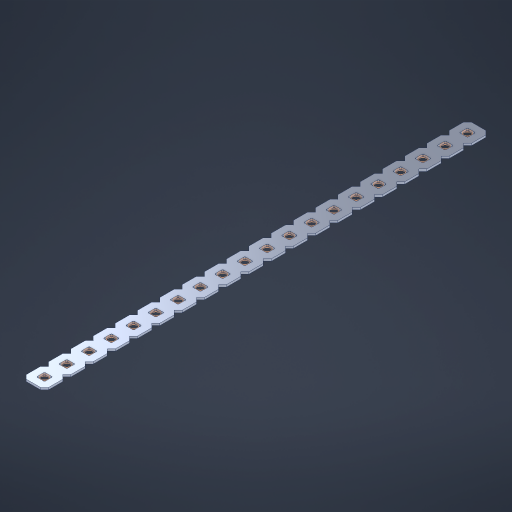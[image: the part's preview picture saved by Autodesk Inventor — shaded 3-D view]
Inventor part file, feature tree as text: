
AUTODESK INVENTOR PART (.ipt)
format: ipt  version: 2023 (Build 270158000, 158)  size: 516,608 bytes
history: native  units: in
note: dims shown in document units (in); Inventor stores cm internally (conversion verified against a paired STEP export)
features: other x21, extrude x19, sketch x2, pattern_linear x1
ambient origin geometry x8: Origin, YZ Plane, XZ Plane, XY Plane, X Axis, Y Axis, Z Axis, Center Point
bodies: Solid1 (feature_tree), Body (feature_tree)
feature tree (43):
  pattern_linear  "Rectangular Pattern1"  Spacing1=0.09in  [1 undecoded]
  sketch  "Sketch1"  dims[d1=0.5in]
  sketch  "Sketch2"  dims[d2=0.182in d3=0.09in d4=0.09in d5=0.09in d6=0.09in d7=0.09in d8=0.09in d9=0.09in d10=0.09in d11=0.02in d13=0.0in d14=0.172in d15=0.0625in d16=0.0in d19=0.5in d22=0.5in]
  other  "Srf1"
  other  "Srf126"
  other  "Srf127"
  other  "Srf128"
  other  "Srf129"
  other  "Srf130"
  other  "Srf131"
  other  "Srf250"
  other  "Srf251"
  other  "Srf252"
  other  "Srf253"
  other  "Srf254"
  other  "Srf255"
  other  "Srf256"
  other  "Srf257"
  other  "Srf258"
  other  "Srf259"
  other  "Srf260"
  other  "Srf261"
  other  "Srf262"
  other  "Circle"
  extrude  "ExtrusionSrf126"  Depth=0.09in
  extrude  "ExtrusionSrf127"  Depth=0.09in
  extrude  "ExtrusionSrf128"  Depth=0.09in
  extrude  "ExtrusionSrf129"  Depth=0.09in
  extrude  "ExtrusionSrf130"  Depth=0.09in
  extrude  "ExtrusionSrf131"  Depth=0.09in
  extrude  "ExtrusionSrf250"  Depth=0.09in
  extrude  "ExtrusionSrf251"  Depth=0.02in
  extrude  "ExtrusionSrf252"  TaperAngle=0.0deg  [1 undecoded]
  extrude  "ExtrusionSrf253"  Depth=0.5in
  extrude  "ExtrusionSrf254"  Depth=0.5in TaperAngle=0.0deg
  extrude  "ExtrusionSrf255"  Depth=0.5in
  extrude  "ExtrusionSrf256"  Depth=0.5in
  extrude  "ExtrusionSrf257"  [1 undecoded]
  extrude  "ExtrusionSrf258"  [1 undecoded]
  extrude  "ExtrusionSrf259"  [1 undecoded]
  extrude  "ExtrusionSrf260"  [1 undecoded]
  extrude  "ExtrusionSrf261"  [1 undecoded]
  extrude  "ExtrusionSrf262"  [1 undecoded]
note: 8 required parameter values undecoded (feature->parameter linkage not recoverable at this tier; creation-order binding heuristic only, values carry confidence <= 0.55)
